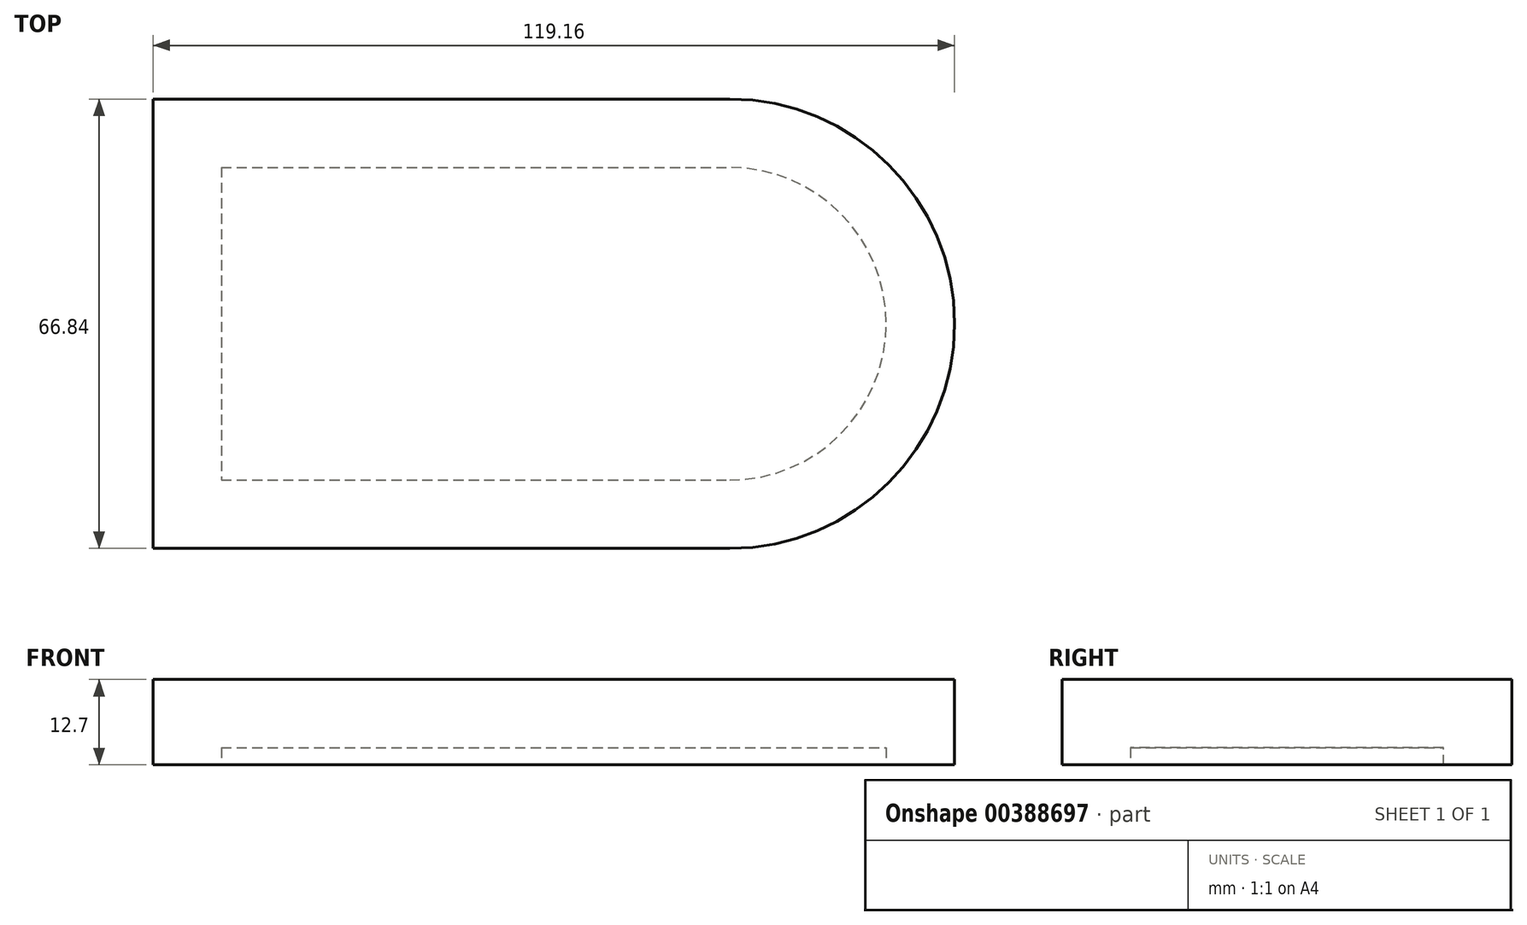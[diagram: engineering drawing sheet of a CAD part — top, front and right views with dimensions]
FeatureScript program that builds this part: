
annotation { "Feature Type Name" : "Feature", "Feature Type Description" : "" }
export const myFeature = defineFeature(function(context is Context, id is Id, definition is map)
    precondition{}
    {
        {
            var Q0;
            Q0=qCreatedBy(makeId("Top.planeOp"),FACE);
            var sketch = newSketch(context, id + "F0", { "sketchPlane" : qUnion([Q0])});
            skLineSegment(sketch, "E0.bottom", {"start": v(-50.78, 47.46) * mm, "end": v(34.96, 47.46) * mm});
            skLineSegment(sketch, "E0.top", {"start": v(-50.78, -19.38) * mm, "end": v(34.96, -19.38) * mm});
            skLineSegment(sketch, "E0.left", {"start": v(-50.78, 47.46) * mm, "end": v(-50.78, -19.38) * mm});
            skLineSegment(sketch, "E0.right", {"start": v(34.96, 47.46) * mm, "end": v(34.96, -19.38) * mm});
            skArc(sketch, "E1", {"start": v(34.96, -19.38) * mm, "mid": v(68.38, 14.04) * mm, "end": v(34.96, 47.46) * mm});
            skSolve(sketch);
        }
        {
            var Q0;
            Q0=makeQuery(id+"F0.imprint","IMPRINT",FACE,{"disambiguationData":[TD([[makeQuery(id+"F0.imprint","IMPRINT",EDGE,{"derivedFrom":sQuery(id+"F0.wireOp",EDGE,"E0.right")}),1.0]])]});
            var Q1;
            Q1=makeQuery(id+"F0.imprint","IMPRINT",FACE,{"disambiguationData":[TD([[makeQuery(id+"F0.imprint","IMPRINT",EDGE,{"derivedFrom":sQuery(id+"F0.wireOp",EDGE,"E0.bottom")}),-1.0]])]});
            extrude(context, id + "F1", {"entities" : qUnion([Q0, Q1]), "depth" : 12.7 * mm});
        }
        {
            var Q0;
            Q0=makeQuery(id+"F1.opExtrude","CAP_FACE",FACE,{"disambiguationData":[OSD([sQuery(id+"F0.wireOp",EDGE,"E0.bottom"),sQuery(id+"F0.wireOp",EDGE,"E0.top"),sQuery(id+"F0.wireOp",EDGE,"E0.left"),sQuery(id+"F0.wireOp",EDGE,"E1")])],"isStart":true});
            shell(context, id + "F2", {"entities" : qUnion([Q0]), "thickness" : 10.16 * mm});
        }
    });
